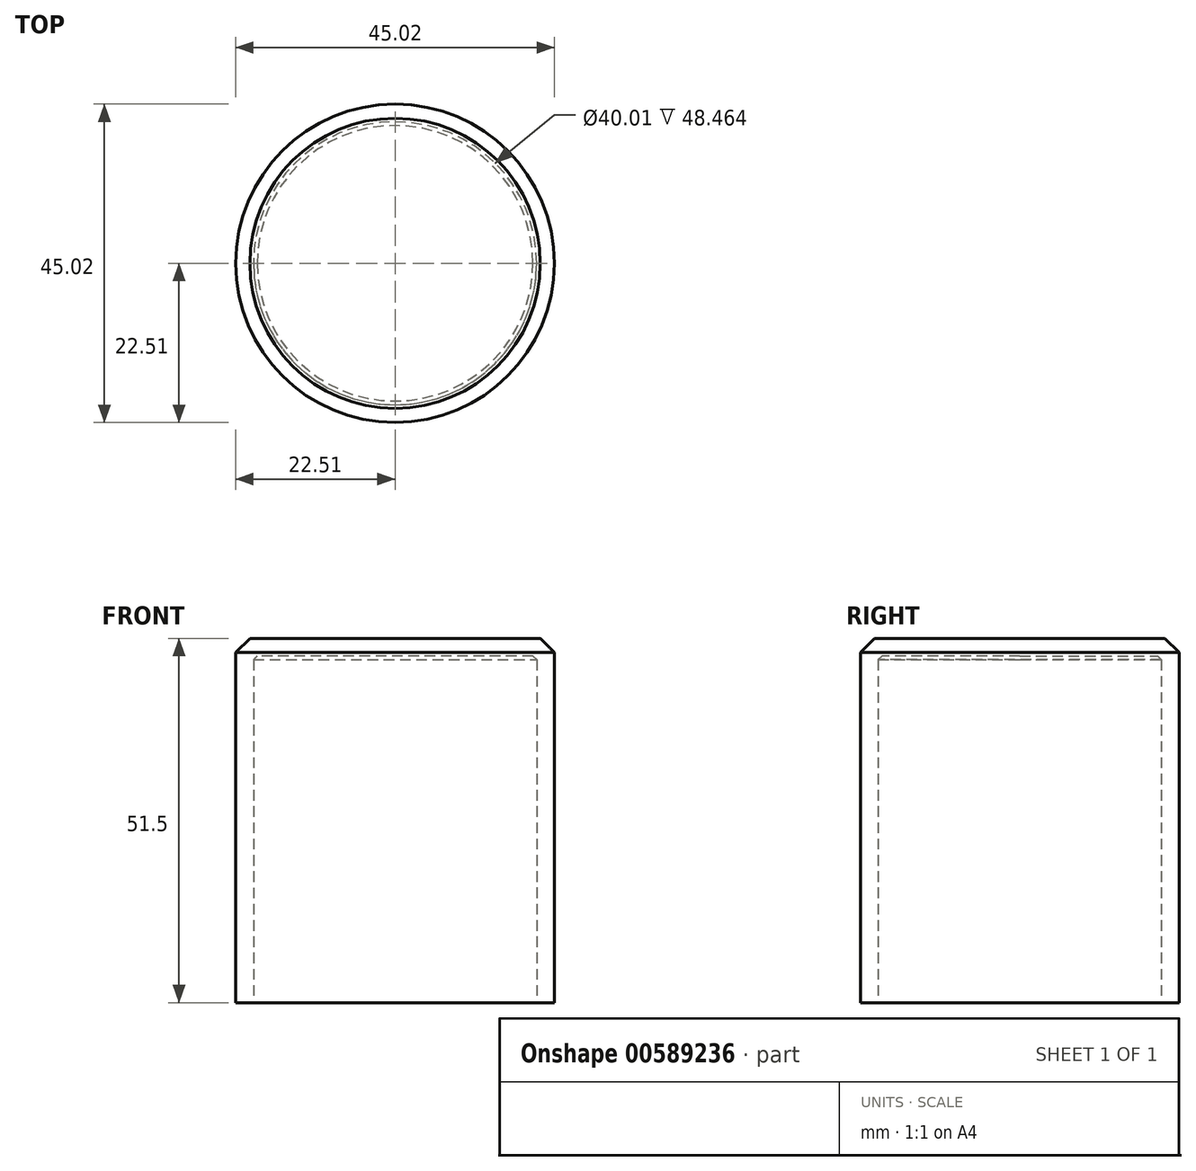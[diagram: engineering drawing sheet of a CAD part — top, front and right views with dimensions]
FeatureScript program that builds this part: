
annotation { "Feature Type Name" : "Feature", "Feature Type Description" : "" }
export const myFeature = defineFeature(function(context is Context, id is Id, definition is map)
    precondition{}
    {
        {
            var Q0;
            Q0=qCreatedBy(makeId("Top.planeOp"),FACE);
            var sketch = newSketch(context, id + "F0", { "sketchPlane" : qUnion([Q0])});
            skCircle(sketch, "E0", {"center": v(0, 0) * mm, "radius": 22.5 * mm});
            skSolve(sketch);
        }
        {
            var Q0;
            Q0=makeQuery(id+"F0.imprint","IMPRINT",FACE,{"disambiguationData":[TD([[makeQuery(id+"F0.imprint","IMPRINT",EDGE,{"derivedFrom":sQuery(id+"F0.wireOp",EDGE,"E0")}),1.0]])]});
            extrude(context, id + "F1", {"entities" : qUnion([Q0]), "depth" : 49.5 * mm, "offsetDistance" : 25 * mm});
        }
        {
            var Q0;
            Q0=makeQuery(id+"F1.opExtrude","CAP_FACE",FACE,{"disambiguationData":[OSD([sQuery(id+"F0.wireOp",EDGE,"E0")])],"isStart":false});
            extrude(context, id + "F2", {"entities" : qUnion([Q0]), "operationType" : NewBodyOperationType.ADD, "depth" : 2 * mm, "offsetDistance" : 25 * mm});
        }
        {
            var Q0;
            Q0=makeQuery(id+"F2.opExtrude","CAP_EDGE",EDGE,{"disambiguationData":[OSD([sQuery(id+"F0.wireOp",EDGE,"E0")])],"isStart":false});
            chamfer(context, id + "F3", {"entities" : qUnion([Q0]), "width" : 2 * mm, "tangentPropagation" : true});
        }
        {
            var Q0;
            Q0=makeQuery(id+"F1.opExtrude","CAP_FACE",FACE,{"disambiguationData":[OSD([sQuery(id+"F0.wireOp",EDGE,"E0")])],"isStart":true});
            shell(context, id + "F4", {"entities" : qUnion([Q0]), "thickness" : 2.5 * mm});
        }
    });
